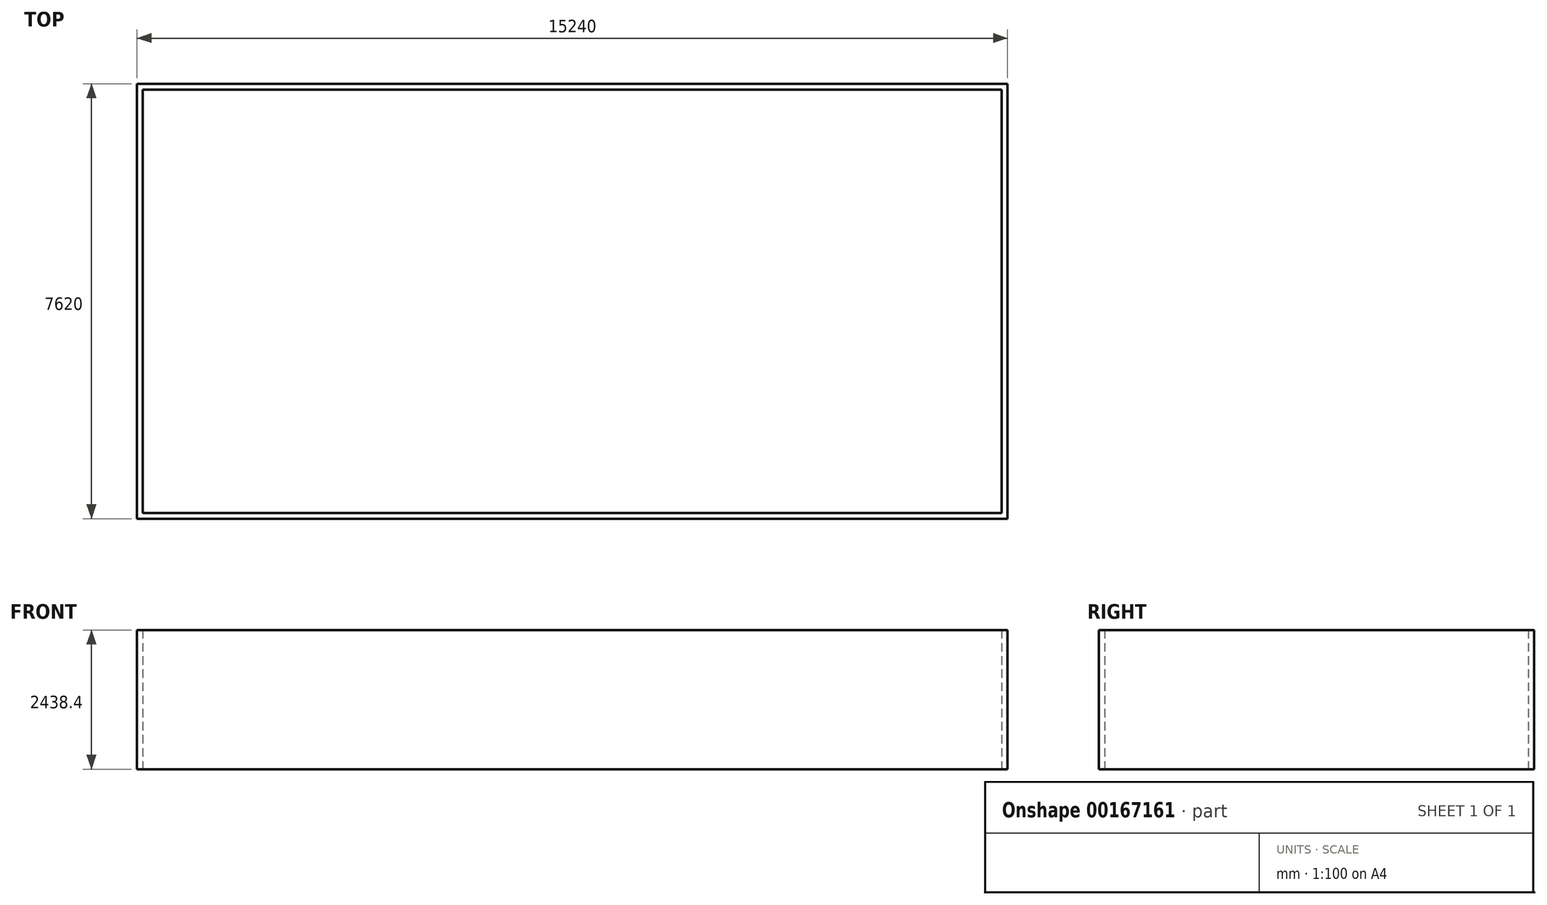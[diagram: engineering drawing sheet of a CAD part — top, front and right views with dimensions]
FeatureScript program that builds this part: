
annotation { "Feature Type Name" : "Feature", "Feature Type Description" : "" }
export const myFeature = defineFeature(function(context is Context, id is Id, definition is map)
    precondition{}
    {
        {
            var Q0;
            Q0=qCreatedBy(makeId("Top.planeOp"),FACE);
            var sketch = newSketch(context, id + "F0", { "sketchPlane" : qUnion([Q0])});
            skLineSegment(sketch, "E0.bottom", {"start": v(7620, -3810) * mm, "end": v(-7620, -3810) * mm});
            skLineSegment(sketch, "E0.top", {"start": v(7620, 3810) * mm, "end": v(-7620, 3810) * mm});
            skLineSegment(sketch, "E0.left", {"start": v(7620, -3810) * mm, "end": v(7620, 3810) * mm});
            skLineSegment(sketch, "E0.right", {"start": v(-7620, -3810) * mm, "end": v(-7620, 3810) * mm});
            skPoint(sketch, "E0.middle", {"position": v(0, 0) * mm});
            skLineSegment(sketch, "E1.0", {"start": v(7518.4, 3708.4) * mm, "end": v(-7518.4, 3708.4) * mm});
            skLineSegment(sketch, "E2.0", {"start": v(-7518.4, -3708.4) * mm, "end": v(-7518.4, 3708.4) * mm});
            skLineSegment(sketch, "E3.0", {"start": v(7518.4, -3708.4) * mm, "end": v(-7518.4, -3708.4) * mm});
            skLineSegment(sketch, "E4.0", {"start": v(7518.4, -3708.4) * mm, "end": v(7518.4, 3708.4) * mm});
            skSolve(sketch);
        }
        {
            var Q0;
            Q0=makeQuery(id+"F0.imprint","IMPRINT",FACE,{"disambiguationData":[TD([[makeQuery(id+"F0.imprint","IMPRINT",EDGE,{"derivedFrom":sQuery(id+"F0.wireOp",EDGE,"E0.bottom")}),-1.0]])]});
            extrude(context, id + "F1", {"entities" : qUnion([Q0]), "depth" : 2438.4 * mm});
        }
    });
